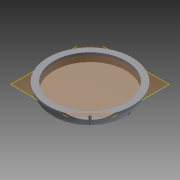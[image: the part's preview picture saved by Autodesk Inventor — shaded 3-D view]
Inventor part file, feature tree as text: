
AUTODESK INVENTOR PART (.ipt)
format: ipt  version: 2014 (Build 180170000, 170)  size: 203,776 bytes
history: native  units: mm
features: sketch x5, extrude x3, fillet x2, plane x1, loft x1
ambient origin geometry x8: Origin, YZ Plane, XZ Plane, XY Plane, X Axis, Y Axis, Z Axis, Center Point
bodies: Solid1 (feature_tree)
feature tree (12):
  sketch  "Sketch1"  dims[d0=120.0mm d1=20.0mm d2=140.0mm]
  plane  "Work Plane1"
  loft  "Loft1"
  fillet  "Fillet1"  Radius=140.0mm
  extrude  "Extrusion1"  TaperAngle=0.0deg  [1 undecoded]
  extrude  "Extrusion2"  Depth=20.0mm
  extrude  "Extrusion3"  Depth=10.0mm
  fillet  "Fillet2"  Radius=4.0mm
  sketch  "Sketch2"  dims[d3=0.0mm d4=90.0deg d5=0.0mm d6=90.0deg]
  sketch  "Sketch3"  dims[d7=20.0mm d8=120.0mm]
  sketch  "Sketch4"  dims[d9=10.0mm d10=0.0mm d11=130.0mm d12=4.0mm]
  sketch  "Sketch5"  dims[d13=4.0mm d14=4.0mm d15=4.0mm d16=45.0deg d17=4.0mm d18=4.0mm d19=4.0mm d20=4.0mm d21=10.0mm d22=0.0mm d23=4.0mm d24=0.0mm d25=20.0mm]
note: 1 required parameter value undecoded (feature->parameter linkage not recoverable at this tier; creation-order binding heuristic only, values carry confidence <= 0.55)
